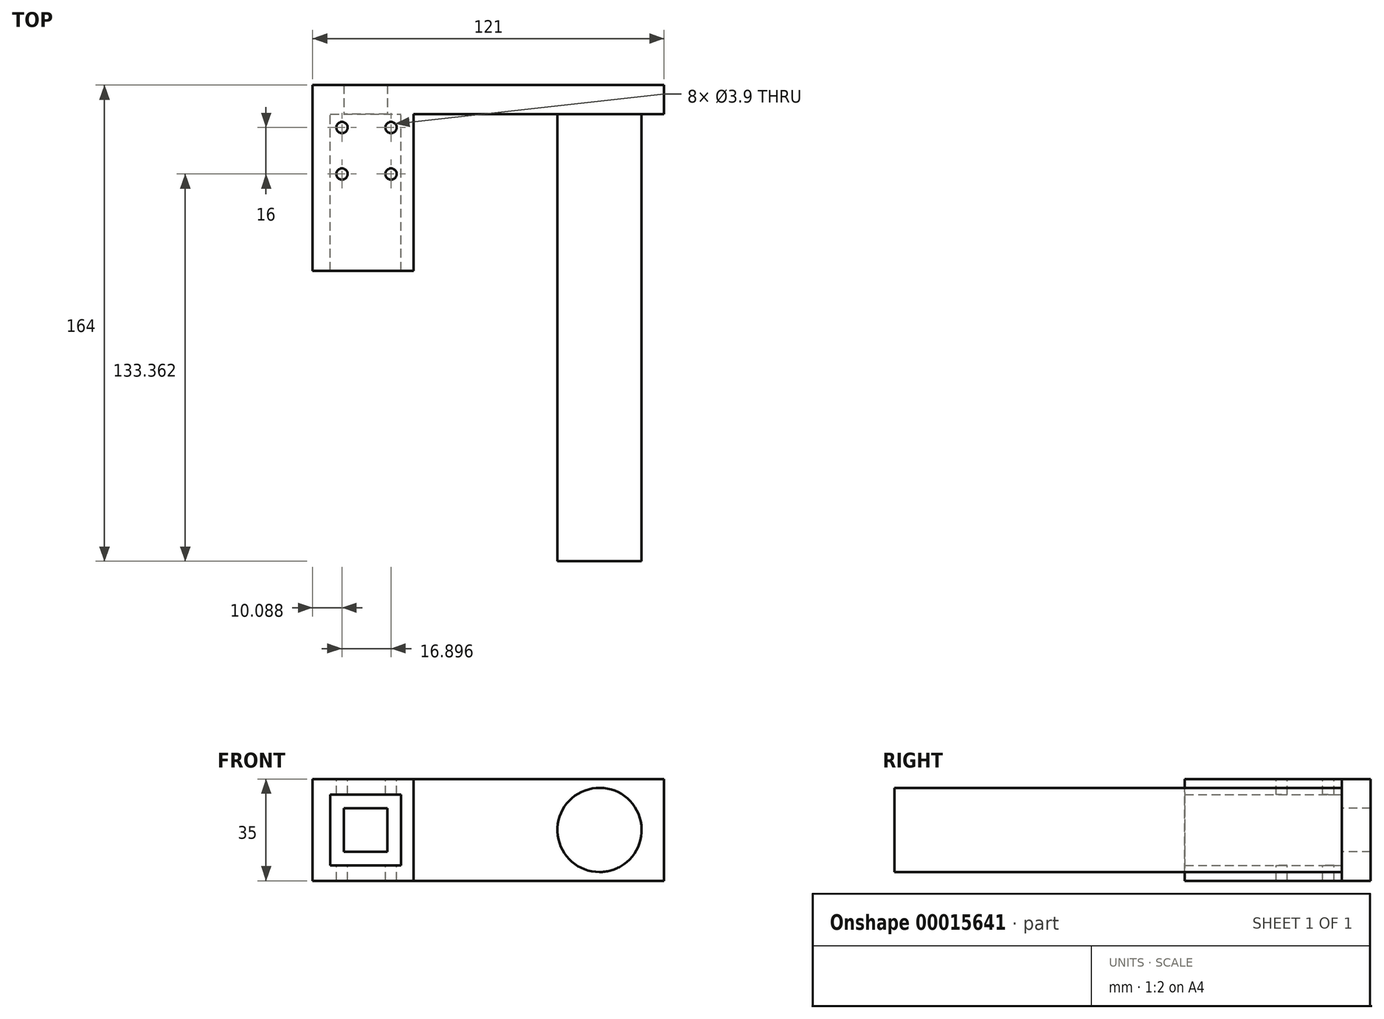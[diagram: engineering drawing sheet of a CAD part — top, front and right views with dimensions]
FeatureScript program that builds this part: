
annotation { "Feature Type Name" : "Feature", "Feature Type Description" : "" }
export const myFeature = defineFeature(function(context is Context, id is Id, definition is map)
    precondition{}
    {
        {
            var Q0;
            Q0=qCreatedBy(makeId("Front.planeOp"),FACE);
            var sketch = newSketch(context, id + "F0", { "sketchPlane" : qUnion([Q0])});
            skLineSegment(sketch, "E0.rect.bottom", {"start": v(-43, 16) * mm, "end": v(43, 16) * mm});
            skLineSegment(sketch, "E0.rect.top", {"start": v(-43, -16) * mm, "end": v(43, -16) * mm});
            skLineSegment(sketch, "E0.rect.left", {"start": v(-43, 16) * mm, "end": v(-43, -16) * mm});
            skLineSegment(sketch, "E0.rect.right", {"start": v(43, 16) * mm, "end": v(43, -16) * mm});
            skPoint(sketch, "E0.rect.middle", {"position": v(0, 0) * mm});
            skSolve(sketch);
        }
        {
            var Q0;
            Q0=makeQuery(id+"F0.imprint","IMPRINT",FACE,{"disambiguationData":[TD([[makeQuery(id+"F0.imprint","IMPRINT",EDGE,{"derivedFrom":sQuery(id+"F0.wireOp",EDGE,"E0.rect.bottom")}),-1.0]])]});
            extrude(context, id + "F1", {"entities" : qUnion([Q0]), "depth" : 10 * mm});
        }
        {
            var Q0;
            Q0=makeQuery(id+"F1.opExtrude","CAP_FACE",FACE,{"disambiguationData":[OSD([sQuery(id+"F0.wireOp",EDGE,"E0.rect.bottom"),sQuery(id+"F0.wireOp",EDGE,"E0.rect.top"),sQuery(id+"F0.wireOp",EDGE,"E0.rect.left"),sQuery(id+"F0.wireOp",EDGE,"E0.rect.right")])],"isStart":false});
            var sketch = newSketch(context, id + "F2", { "sketchPlane" : qUnion([Q0])});
            skSolve(sketch);
        }
        {
            var Q0;
            Q0=makeQuery(id+"F2.imprint","IMPRINT",FACE,{"disambiguationData":[TD([[makeQuery(id+"F2.imprint","IMPRINT",EDGE,{"derivedFrom":makeQuery(id+"F1.opExtrude","CAP_EDGE",EDGE,{"disambiguationData":[OSD([sQuery(id+"F0.wireOp",EDGE,"E0.rect.bottom")])],"isStart":false})}),-1.0]])]});
            var sketch = newSketch(context, id + "F3", { "sketchPlane" : qUnion([Q0])});
            skCircle(sketch, "E1", {"center": v(55.78, 0) * mm, "radius": 14.5 * mm});
            skSolve(sketch);
        }
        {
            var Q0;
            Q0 = qSketchRegion(id + "F3", true);
            extrude(context, id + "F4", {"entities" : qUnion([Q0]), "operationType" : NewBodyOperationType.ADD, "depth" : 92.4 * mm});
        }
        {
            var Q0;
            Q0=makeQuery(id+"F1.opExtrude","SWEPT_FACE",FACE,{"disambiguationData":[OSD([sQuery(id+"F0.wireOp",EDGE,"E0.rect.top")])]});
            extrude(context, id + "F5", {"entities" : qUnion([Q0]), "operationType" : NewBodyOperationType.ADD, "depth" : 1.5 * mm});
        }
        {
            var Q0;
            Q0=makeQuery(id+"F1.opExtrude","SWEPT_FACE",FACE,{"disambiguationData":[OSD([sQuery(id+"F0.wireOp",EDGE,"E0.rect.bottom")])]});
            extrude(context, id + "F6", {"entities" : qUnion([Q0]), "operationType" : NewBodyOperationType.ADD, "depth" : 1.5 * mm});
        }
        {
            var Q0;
            Q0=makeQuery(id+"F2.imprint","IMPRINT",FACE,{"disambiguationData":[TD([[makeQuery(id+"F2.imprint","IMPRINT",EDGE,{"derivedFrom":makeQuery(id+"F1.opExtrude","CAP_EDGE",EDGE,{"disambiguationData":[OSD([sQuery(id+"F0.wireOp",EDGE,"E0.rect.bottom")])],"isStart":false})}),-1.0]])]});
            var sketch = newSketch(context, id + "F7", { "sketchPlane" : qUnion([Q0])});
            skPoint(sketch, "E2.rect.middle", {"position": v(-24.74, 0) * mm});
            skLineSegment(sketch, "E3.rect.bottom", {"start": v(-17.24, -7.5) * mm, "end": v(-32.24, -7.5) * mm});
            skLineSegment(sketch, "E3.rect.top", {"start": v(-17.24, 7.5) * mm, "end": v(-32.24, 7.5) * mm});
            skLineSegment(sketch, "E3.rect.left", {"start": v(-17.24, -7.5) * mm, "end": v(-17.24, 7.5) * mm});
            skLineSegment(sketch, "E3.rect.right", {"start": v(-32.24, -7.5) * mm, "end": v(-32.24, 7.5) * mm});
            skSolve(sketch);
        }
        {
            var Q0;
            {var subQ0=sQuery(id+"F0.wireOp",EDGE,"E0.rect.bottom");var subQ1=sQuery(id+"F0.wireOp",EDGE,"E0.rect.top");var subQ2=sQuery(id+"F0.wireOp",EDGE,"E0.rect.left");var subQ3=sQuery(id+"F0.wireOp",EDGE,"E0.rect.right");Q0=makeQuery(id+"FknnuqSdBrIK8F0_1.boolean.opBoolean","SPLIT",FACE,{"disambiguationData":[TD([makeQuery(id+"F1.opExtrude","SWEPT_FACE",FACE,{"disambiguationData":[OSD([subQ2])]})])],"derivedFrom":makeQuery(id+"F6.boolean.opBoolean","MERGE",FACE,{"derivedFrom":[makeQuery(id+"F5.boolean.opBoolean","MERGE",FACE,{"derivedFrom":[makeQuery(id+"F1.opExtrude","CAP_FACE",FACE,{"disambiguationData":[OSD([subQ0,subQ1,subQ2,subQ3])],"isStart":false}),makeQuery(id+"F5.opExtrude","SWEPT_FACE",FACE,{"disambiguationData":[OSD([subQ1]),TDD([makeQuery(id+"F1.opExtrude","CAP_EDGE",EDGE,{"disambiguationData":[OSD([subQ1])],"isStart":false})])]})]}),makeQuery(id+"F6.opExtrude","SWEPT_FACE",FACE,{"disambiguationData":[OSD([subQ0]),TDD([makeQuery(id+"F1.opExtrude","CAP_EDGE",EDGE,{"disambiguationData":[OSD([subQ0])],"isStart":false})])]})]})});}
            var sketch = newSketch(context, id + "F8", { "sketchPlane" : qUnion([Q0])});
            skLineSegment(sketch, "E4.bottom", {"start": v(-43, -17.5) * mm, "end": v(-12.54, -17.5) * mm});
            skLineSegment(sketch, "E4.top", {"start": v(-43, -12.2) * mm, "end": v(-12.54, -12.2) * mm});
            skLineSegment(sketch, "E4.left", {"start": v(-43, -17.5) * mm, "end": v(-43, -12.2) * mm});
            skLineSegment(sketch, "E4.right", {"start": v(-12.54, -17.5) * mm, "end": v(-12.54, -12.2) * mm});
            skLineSegment(sketch, "E5.bottom", {"start": v(-12.54, -17.5) * mm, "end": v(-8.25, -17.5) * mm});
            skLineSegment(sketch, "E5.top", {"start": v(-12.54, 17.5) * mm, "end": v(-8.25, 17.5) * mm});
            skLineSegment(sketch, "E5.left", {"start": v(-12.54, -17.5) * mm, "end": v(-12.54, 17.5) * mm});
            skLineSegment(sketch, "E5.right", {"start": v(-8.25, -17.5) * mm, "end": v(-8.25, 17.5) * mm});
            skLineSegment(sketch, "E6.bottom", {"start": v(-12.54, 17.5) * mm, "end": v(-43, 17.5) * mm});
            skLineSegment(sketch, "E6.top", {"start": v(-12.54, 12.2) * mm, "end": v(-43, 12.2) * mm});
            skLineSegment(sketch, "E6.left", {"start": v(-12.54, 17.5) * mm, "end": v(-12.54, 12.2) * mm});
            skLineSegment(sketch, "E6.right", {"start": v(-43, 17.5) * mm, "end": v(-43, 12.2) * mm});
            skLineSegment(sketch, "E7.bottom", {"start": v(-43, 12.2) * mm, "end": v(-36.94, 12.2) * mm});
            skLineSegment(sketch, "E7.top", {"start": v(-43, -12.2) * mm, "end": v(-36.94, -12.2) * mm});
            skLineSegment(sketch, "E7.left", {"start": v(-43, 12.2) * mm, "end": v(-43, -12.2) * mm});
            skLineSegment(sketch, "E7.right", {"start": v(-36.94, 12.2) * mm, "end": v(-36.94, -12.2) * mm});
            skSolve(sketch);
        }
        {
            var Q0;
            Q0 = qSketchRegion(id + "F8", true);
            extrude(context, id + "F9", {"entities" : qUnion([Q0]), "operationType" : NewBodyOperationType.ADD, "depth" : 40 * mm});
        }
        {
            var Q0;
            Q0=makeQuery(id+"F9.boolean.opBoolean","MERGE",FACE,{"derivedFrom":[makeQuery(id+"F6.opExtrude","CAP_FACE",FACE,{"disambiguationData":[OSD([sQuery(id+"F0.wireOp",EDGE,"E0.rect.bottom")])],"isStart":false}),makeQuery(id+"F9.opExtrude","SWEPT_FACE",FACE,{"disambiguationData":[OSD([sQuery(id+"F8.wireOp",EDGE,"E5.top"),sQuery(id+"F8.wireOp",EDGE,"E6.bottom")])]})]});
            var sketch = newSketch(context, id + "F10", { "sketchPlane" : qUnion([Q0])});
            skSolve(sketch);
        }
        {
            var Q0;
            {var subQ0=sQuery(id+"F0.wireOp",EDGE,"E0.rect.bottom");Q0=makeQuery(id+"F10.imprint","IMPRINT",FACE,{"disambiguationData":[TD([[makeQuery(id+"F10.imprint","IMPRINT",EDGE,{"derivedFrom":makeQuery(id+"F6.opExtrude","CAP_EDGE",EDGE,{"disambiguationData":[OSD([subQ0]),TDD([makeQuery(id+"F1.opExtrude","CAP_EDGE",EDGE,{"disambiguationData":[OSD([subQ0])],"isStart":true})])],"isStart":false})}),-1.0]])]});}
            var sketch = newSketch(context, id + "F11", { "sketchPlane" : qUnion([Q0])});
            skCircle(sketch, "E8", {"center": v(-32.91, -14.64) * mm, "radius": 1.95 * mm});
            skCircle(sketch, "E9.MirrorC", {"center": v(-16.02, -14.64) * mm, "radius": 1.95 * mm});
            skCircle(sketch, "E10", {"center": v(-32.91, -30.64) * mm, "radius": 1.95 * mm});
            skCircle(sketch, "E11", {"center": v(-16.02, -30.64) * mm, "radius": 1.95 * mm});
            skSolve(sketch);
        }
        {
            var Q0;
            Q0 = qSketchRegion(id + "F11", true);
            extrude(context, id + "F12", {"entities" : qUnion([Q0]), "operationType" : NewBodyOperationType.REMOVE, "oppositeDirection" : true, "depth" : 37.54 * mm});
        }
        {
            var Q0;
            Q0=makeQuery(id+"F7.imprint","IMPRINT",FACE,{"disambiguationData":[TD([[makeQuery(id+"F7.imprint","IMPRINT",EDGE,{"derivedFrom":sQuery(id+"F7.wireOp",EDGE,"E3.rect.bottom")}),-1.0]])]});
            extrude(context, id + "F13", {"entities" : qUnion([Q0]), "operationType" : NewBodyOperationType.REMOVE, "oppositeDirection" : true, "depth" : 25 * mm});
        }
        {
            var Q0;
            Q0=makeQuery(id+"F4.opExtrude","CAP_FACE",FACE,{"disambiguationData":[OSD([sQuery(id+"F3.wireOp",EDGE,"E1")])],"isStart":false});
            extrude(context, id + "F14", {"entities" : qUnion([Q0]), "operationType" : NewBodyOperationType.ADD, "depth" : 24.6 * mm});
        }
        {
            var Q0;
            Q0=makeQuery(id+"F9.opExtrude","CAP_FACE",FACE,{"disambiguationData":[OSD([sQuery(id+"F8.wireOp",EDGE,"E4.bottom"),sQuery(id+"F8.wireOp",EDGE,"E4.top"),sQuery(id+"F8.wireOp",EDGE,"E4.left"),sQuery(id+"F8.wireOp",EDGE,"E5.bottom"),sQuery(id+"F8.wireOp",EDGE,"E5.top"),sQuery(id+"F8.wireOp",EDGE,"E5.left"),sQuery(id+"F8.wireOp",EDGE,"E5.right"),sQuery(id+"F8.wireOp",EDGE,"E6.bottom"),sQuery(id+"F8.wireOp",EDGE,"E6.top"),sQuery(id+"F8.wireOp",EDGE,"E6.right"),sQuery(id+"F8.wireOp",EDGE,"E7.left"),sQuery(id+"F8.wireOp",EDGE,"E7.right")])],"isStart":false});
            extrude(context, id + "F15", {"entities" : qUnion([Q0]), "operationType" : NewBodyOperationType.ADD, "depth" : 24 * mm});
        }
        {
            var Q0;
            Q0=makeQuery(id+"F14.opExtrude","CAP_FACE",FACE,{"disambiguationData":[OSD([sQuery(id+"F3.wireOp",EDGE,"E1")])],"isStart":false});
            extrude(context, id + "F16", {"entities" : qUnion([Q0]), "operationType" : NewBodyOperationType.ADD, "depth" : 34 * mm});
        }
        {
            var Q0;
            Q0=makeQuery(id+"F16.opExtrude","CAP_FACE",FACE,{"disambiguationData":[OSD([sQuery(id+"F3.wireOp",EDGE,"E1")])],"isStart":false});
            extrude(context, id + "F17", {"entities" : qUnion([Q0]), "operationType" : NewBodyOperationType.ADD, "depth" : 3 * mm});
        }
        {
            var Q0;
            Q0=makeQuery(id+"F15.opExtrude","CAP_FACE",FACE,{"disambiguationData":[OSD([sQuery(id+"F8.wireOp",EDGE,"E4.bottom"),sQuery(id+"F8.wireOp",EDGE,"E4.top"),sQuery(id+"F8.wireOp",EDGE,"E4.left"),sQuery(id+"F8.wireOp",EDGE,"E5.bottom"),sQuery(id+"F8.wireOp",EDGE,"E5.top"),sQuery(id+"F8.wireOp",EDGE,"E5.left"),sQuery(id+"F8.wireOp",EDGE,"E5.right"),sQuery(id+"F8.wireOp",EDGE,"E6.bottom"),sQuery(id+"F8.wireOp",EDGE,"E6.top"),sQuery(id+"F8.wireOp",EDGE,"E6.right"),sQuery(id+"F8.wireOp",EDGE,"E7.left"),sQuery(id+"F8.wireOp",EDGE,"E7.right")])],"isStart":false});
            var sketch = newSketch(context, id + "F18", { "sketchPlane" : qUnion([Q0])});
            skSolve(sketch);
        }
        {
            var Q0;
            Q0 = qSketchRegion(id + "F18", true);
            var Q1;
            Q1=makeQuery(id+"F18.imprint","IMPRINT",FACE,{"disambiguationData":[TD([[makeQuery(id+"F18.imprint","IMPRINT",EDGE,{"derivedFrom":makeQuery(id+"F15.opExtrude","CAP_EDGE",EDGE,{"disambiguationData":[OSD([sQuery(id+"F8.wireOp",EDGE,"E4.top")])],"isStart":false})}),-1.0]])]});
            extrude(context, id + "F19", {"entities" : qUnion([Q0, Q1]), "operationType" : NewBodyOperationType.REMOVE, "oppositeDirection" : true, "depth" : 10 * mm});
        }
        {
            var Q0;
            {var subQ0=sQuery(id+"F0.wireOp",EDGE,"E0.rect.right");Q0=makeQuery(id+"F6.boolean.opBoolean","MERGE",FACE,{"derivedFrom":[makeQuery(id+"F5.boolean.opBoolean","MERGE",FACE,{"derivedFrom":[makeQuery(id+"F1.opExtrude","SWEPT_FACE",FACE,{"disambiguationData":[OSD([subQ0])]}),makeQuery(id+"F5.opExtrude","SWEPT_FACE",FACE,{"disambiguationData":[OSD([sQuery(id+"F0.wireOp",EDGE,"E0.rect.top"),subQ0])]})]}),makeQuery(id+"F6.opExtrude","SWEPT_FACE",FACE,{"disambiguationData":[OSD([sQuery(id+"F0.wireOp",EDGE,"E0.rect.bottom"),subQ0])]})]});}
            extrude(context, id + "F20", {"entities" : qUnion([Q0]), "operationType" : NewBodyOperationType.ADD, "depth" : 10 * mm});
        }
        {
            var Q0;
            Q0=makeQuery(id+"F20.opExtrude","CAP_FACE",FACE,{"disambiguationData":[OSD([sQuery(id+"F0.wireOp",EDGE,"E0.rect.bottom"),sQuery(id+"F0.wireOp",EDGE,"E0.rect.top"),sQuery(id+"F0.wireOp",EDGE,"E0.rect.right")])],"isStart":false});
            extrude(context, id + "F21", {"entities" : qUnion([Q0]), "operationType" : NewBodyOperationType.ADD, "depth" : 10 * mm});
        }
        {
            var Q0;
            Q0=makeQuery(id+"F21.opExtrude","CAP_FACE",FACE,{"disambiguationData":[OSD([sQuery(id+"F0.wireOp",EDGE,"E0.rect.bottom"),sQuery(id+"F0.wireOp",EDGE,"E0.rect.top"),sQuery(id+"F0.wireOp",EDGE,"E0.rect.right")])],"isStart":false});
            extrude(context, id + "F22", {"entities" : qUnion([Q0]), "operationType" : NewBodyOperationType.ADD, "depth" : 15 * mm});
        }
    });
